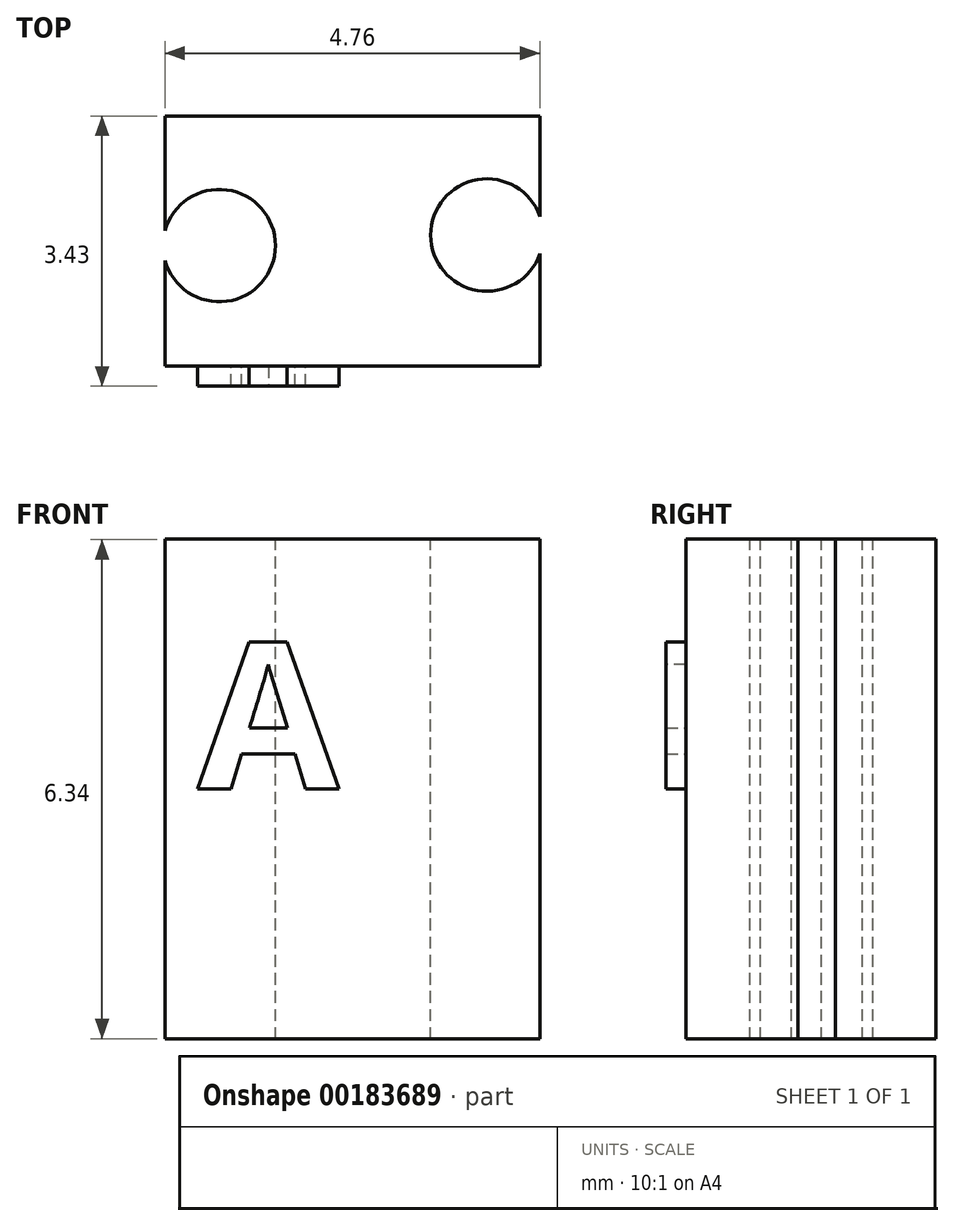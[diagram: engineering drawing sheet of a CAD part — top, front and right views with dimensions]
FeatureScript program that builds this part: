
annotation { "Feature Type Name" : "Feature", "Feature Type Description" : "" }
export const myFeature = defineFeature(function(context is Context, id is Id, definition is map)
    precondition{}
    {
        {
            var Q0;
            Q0=qCreatedBy(makeId("Front.planeOp"),FACE);
            var sketch = newSketch(context, id + "F0", { "sketchPlane" : qUnion([Q0])});
            skLineSegment(sketch, "E0.bottom", {"start": v(2.38, 3.18) * mm, "end": v(-2.38, 3.18) * mm});
            skLineSegment(sketch, "E0.top", {"start": v(2.38, -3.17) * mm, "end": v(-2.38, -3.17) * mm});
            skLineSegment(sketch, "E0.left", {"start": v(2.38, 3.18) * mm, "end": v(2.38, -3.17) * mm});
            skLineSegment(sketch, "E0.right", {"start": v(-2.38, 3.18) * mm, "end": v(-2.38, -3.17) * mm});
            skPoint(sketch, "E0.middle", {"position": v(0, 0) * mm});
            skSolve(sketch);
        }
        {
            var Q0;
            Q0 = qSketchRegion(id + "F0", true);
            extrude(context, id + "F1", {"entities" : qUnion([Q0]), "depth" : 3.17 * mm});
        }
        {
            var Q0;
            Q0=makeQuery(id+"F1.opExtrude","SWEPT_FACE",FACE,{"disambiguationData":[OSD([sQuery(id+"F0.wireOp",EDGE,"E0.bottom")])]});
            var sketch = newSketch(context, id + "F2", { "sketchPlane" : qUnion([Q0])});
            skLineSegment(sketch, "E1", {"start": v(0, 0) * mm, "end": v(0, -3.18) * mm});
            skSolve(sketch);
        }
        {
            var Q0;
            {var subQ0=sQuery(id+"F2.wireOp",EDGE,"E1");Q0=makeQuery(id+"F2.imprint","IMPRINT",FACE,{"disambiguationData":[TD([[makeQuery(id+"F2.imprint","IMPRINT",EDGE,{"derivedFrom":subQ0}),-1.0]])]});}
            var sketch = newSketch(context, id + "F3", { "sketchPlane" : qUnion([Q0])});
            skPoint(sketch, "E2", {"position": v(-1.7, -1.64) * mm});
            skSolve(sketch);
        }
        {
            var Q0;
            Q0=sQuery(id+"F3.wireOp",VERTEX,"E2");
            var Q1;
            Q1=makeQuery(id+"F1.opExtrude","SWEPT_BODY",BODY,{"disambiguationData":[OSD([sQuery(id+"F0.wireOp",EDGE,"E0.bottom"),sQuery(id+"F0.wireOp",EDGE,"E0.top"),sQuery(id+"F0.wireOp",EDGE,"E0.left"),sQuery(id+"F0.wireOp",EDGE,"E0.right")])]});
            hole(context, id + "F4", {"style" : HoleStyle.SIMPLE, "endStyle" : HoleEndStyle.THROUGH, "holeDiameter" : 1.43 * mm, "startFromSketch" : true, "locations" : qUnion([Q0]), "scope" : qUnion([Q1]), "isTappedThrough" : true});
        }
        {
            var Q0;
            {var subQ0=sQuery(id+"F2.wireOp",EDGE,"E1");Q0=makeQuery(id+"F2.imprint","IMPRINT",FACE,{"disambiguationData":[TD([[makeQuery(id+"F2.imprint","IMPRINT",EDGE,{"derivedFrom":subQ0}),1.0]])]});}
            var sketch = newSketch(context, id + "F5", { "sketchPlane" : qUnion([Q0])});
            skPoint(sketch, "E3", {"position": v(1.7, -1.51) * mm});
            skSolve(sketch);
        }
        {
            var Q0;
            Q0=sQuery(id+"F5.wireOp",VERTEX,"E3");
            var Q1;
            Q1=makeQuery(id+"F1.opExtrude","SWEPT_BODY",BODY,{"disambiguationData":[OSD([sQuery(id+"F0.wireOp",EDGE,"E0.bottom"),sQuery(id+"F0.wireOp",EDGE,"E0.top"),sQuery(id+"F0.wireOp",EDGE,"E0.left"),sQuery(id+"F0.wireOp",EDGE,"E0.right")])]});
            hole(context, id + "F6", {"style" : HoleStyle.SIMPLE, "endStyle" : HoleEndStyle.THROUGH, "holeDiameter" : 1.43 * mm, "startFromSketch" : true, "locations" : qUnion([Q0]), "scope" : qUnion([Q1]), "isTappedThrough" : true});
        }
        {
            var Q0;
            Q0=makeQuery(id+"F1.opExtrude","CAP_FACE",FACE,{"disambiguationData":[OSD([sQuery(id+"F0.wireOp",EDGE,"E0.bottom"),sQuery(id+"F0.wireOp",EDGE,"E0.top"),sQuery(id+"F0.wireOp",EDGE,"E0.left"),sQuery(id+"F0.wireOp",EDGE,"E0.right")])],"isStart":false});
            var sketch = newSketch(context, id + "F7", { "sketchPlane" : qUnion([Q0])});
            skText(sketch, "E4", { "text": "A", "fontName": "OpenSans-Bold.ttf"});
            const initialGuessF7  = {"E4": [-0.00197, 0, 1, 0, 0.00188]};
            skSetInitialGuess(sketch, initialGuessF7);
            skSolve(sketch);
        }
        {
            var Q0;
            Q0 = qSketchRegion(id + "F7", true);
            extrude(context, id + "F8", {"entities" : qUnion([Q0]), "operationType" : NewBodyOperationType.ADD, "depth" : 0.25 * mm});
        }
        {
            var Q0;
            {var subQ0=sQuery(id+"F0.wireOp",EDGE,"E0.bottom");var subQ1=sQuery(id+"F0.wireOp",EDGE,"E0.top");var subQ2=sQuery(id+"F0.wireOp",EDGE,"E0.left");var subQ3=sQuery(id+"F0.wireOp",EDGE,"E0.right");Q0=makeQuery(id+"F8.boolean.opBoolean","SPLIT",FACE,{"disambiguationData":[TD([makeQuery(id+"F1.opExtrude","SWEPT_FACE",FACE,{"disambiguationData":[OSD([subQ0])]})])],"derivedFrom":makeQuery(id+"F1.opExtrude","CAP_FACE",FACE,{"disambiguationData":[OSD([subQ0,subQ1,subQ2,subQ3])],"isStart":false})});}
            var sketch = newSketch(context, id + "F9", { "sketchPlane" : qUnion([Q0])});
            skText(sketch, "E5", { "text": "W", "fontName": "OpenSans-Bold.ttf"});
            const initialGuessF9  = {"E5": [0, -0.00157, 1, 0, 0.00157]};
            skSetInitialGuess(sketch, initialGuessF9);
            skSolve(sketch);
        }
        {
            var Q0;
            Q0 = qConstructionFilter(qBodyType(qCreatedBy(id + "F9" ,EDGE), BodyType.WIRE), ConstructionObject.NO);
            extrude(context, id + "F10", {"bodyType" : ToolBodyType.SURFACE, "surfaceEntities" : qUnion([Q0]), "depth" : 0.25 * mm});
        }
    });
